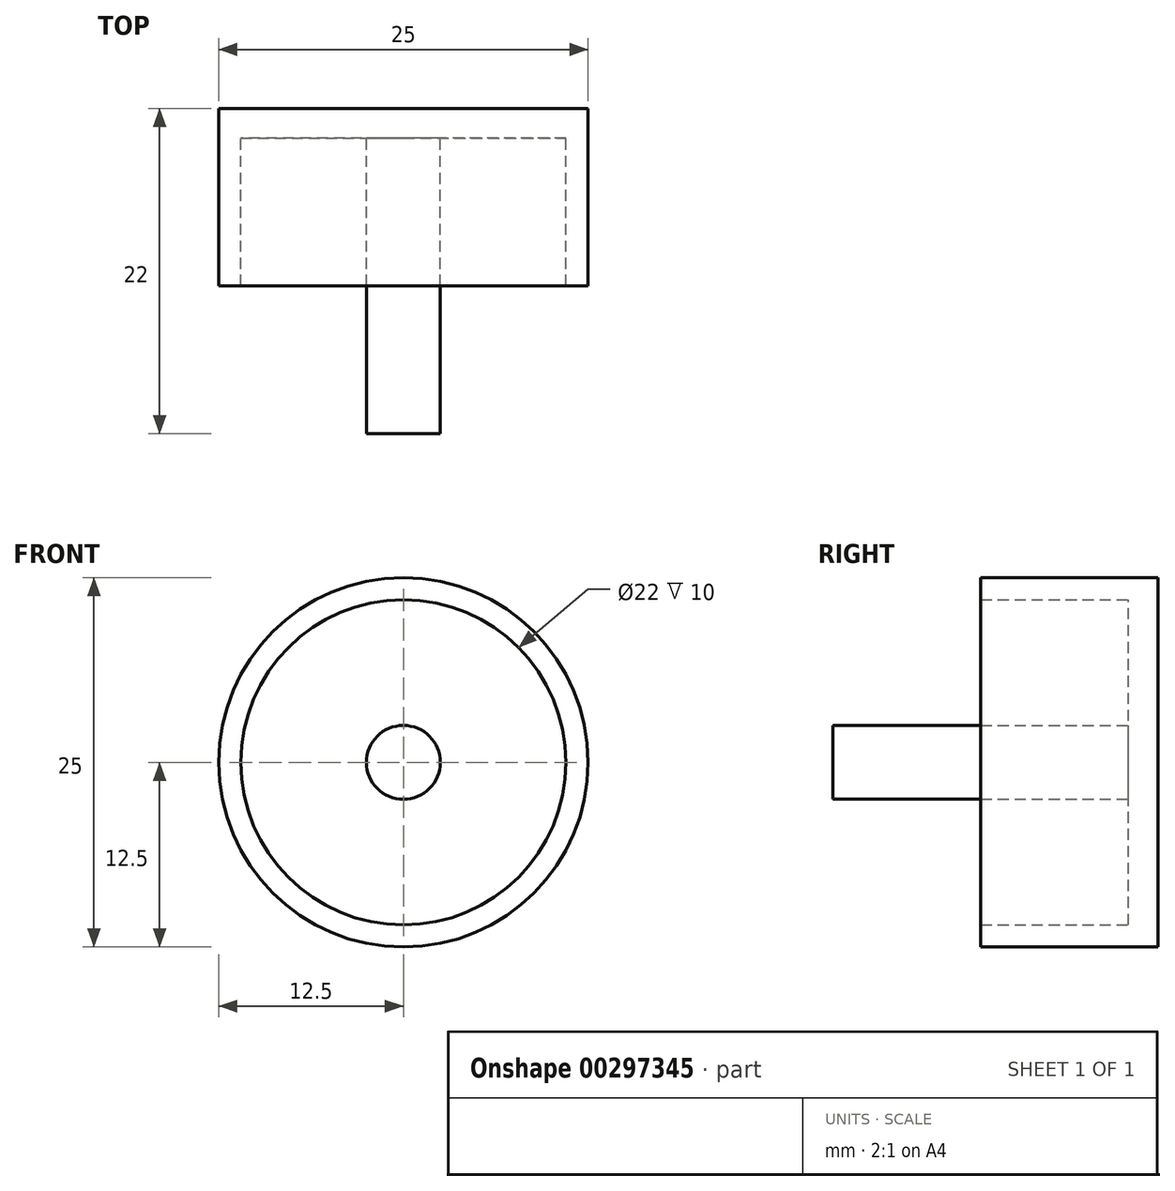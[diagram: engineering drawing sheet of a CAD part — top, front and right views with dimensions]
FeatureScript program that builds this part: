
annotation { "Feature Type Name" : "Feature", "Feature Type Description" : "" }
export const myFeature = defineFeature(function(context is Context, id is Id, definition is map)
    precondition{}
    {
        {
            var Q0;
            Q0=qCreatedBy(makeId("Front.planeOp"),FACE);
            var sketch = newSketch(context, id + "F0", { "sketchPlane" : qUnion([Q0])});
            skCircle(sketch, "E0", {"center": v(0, 0) * mm, "radius": 12.5 * mm});
            skSolve(sketch);
        }
        {
            var Q0;
            Q0=qSketchRegion(id+"F0",true);
            extrude(context, id + "F1", {"entities" : qUnion([Q0]), "depth" : 2 * mm});
        }
        {
            var Q0;
            Q0=makeQuery(id+"F1.opExtrude","CAP_FACE",FACE,{"disambiguationData":[OSD([sQuery(id+"F0.wireOp",EDGE,"E0")])],"isStart":false});
            var sketch = newSketch(context, id + "F2", { "sketchPlane" : qUnion([Q0])});
            skCircle(sketch, "E1", {"center": v(0, 0) * mm, "radius": 12.5 * mm});
            skCircle(sketch, "E2", {"center": v(0, 0) * mm, "radius": 11 * mm});
            skSolve(sketch);
        }
        {
            var Q0;
            Q0=qSketchRegion(id+"F2",true);
            extrude(context, id + "F3", {"entities" : qUnion([Q0]), "operationType" : NewBodyOperationType.ADD, "depth" : 10 * mm});
        }
        {
            var Q0;
            Q0=makeQuery(id+"F1.opExtrude","CAP_FACE",FACE,{"disambiguationData":[OSD([sQuery(id+"F0.wireOp",EDGE,"E0")])],"isStart":false});
            var sketch = newSketch(context, id + "F4", { "sketchPlane" : qUnion([Q0])});
            skCircle(sketch, "E3", {"center": v(0, 0) * mm, "radius": 2.5 * mm});
            skSolve(sketch);
        }
        {
            var Q0;
            Q0=qSketchRegion(id+"F4",true);
            extrude(context, id + "F5", {"entities" : qUnion([Q0]), "operationType" : NewBodyOperationType.ADD, "depth" : 20 * mm});
        }
    });
